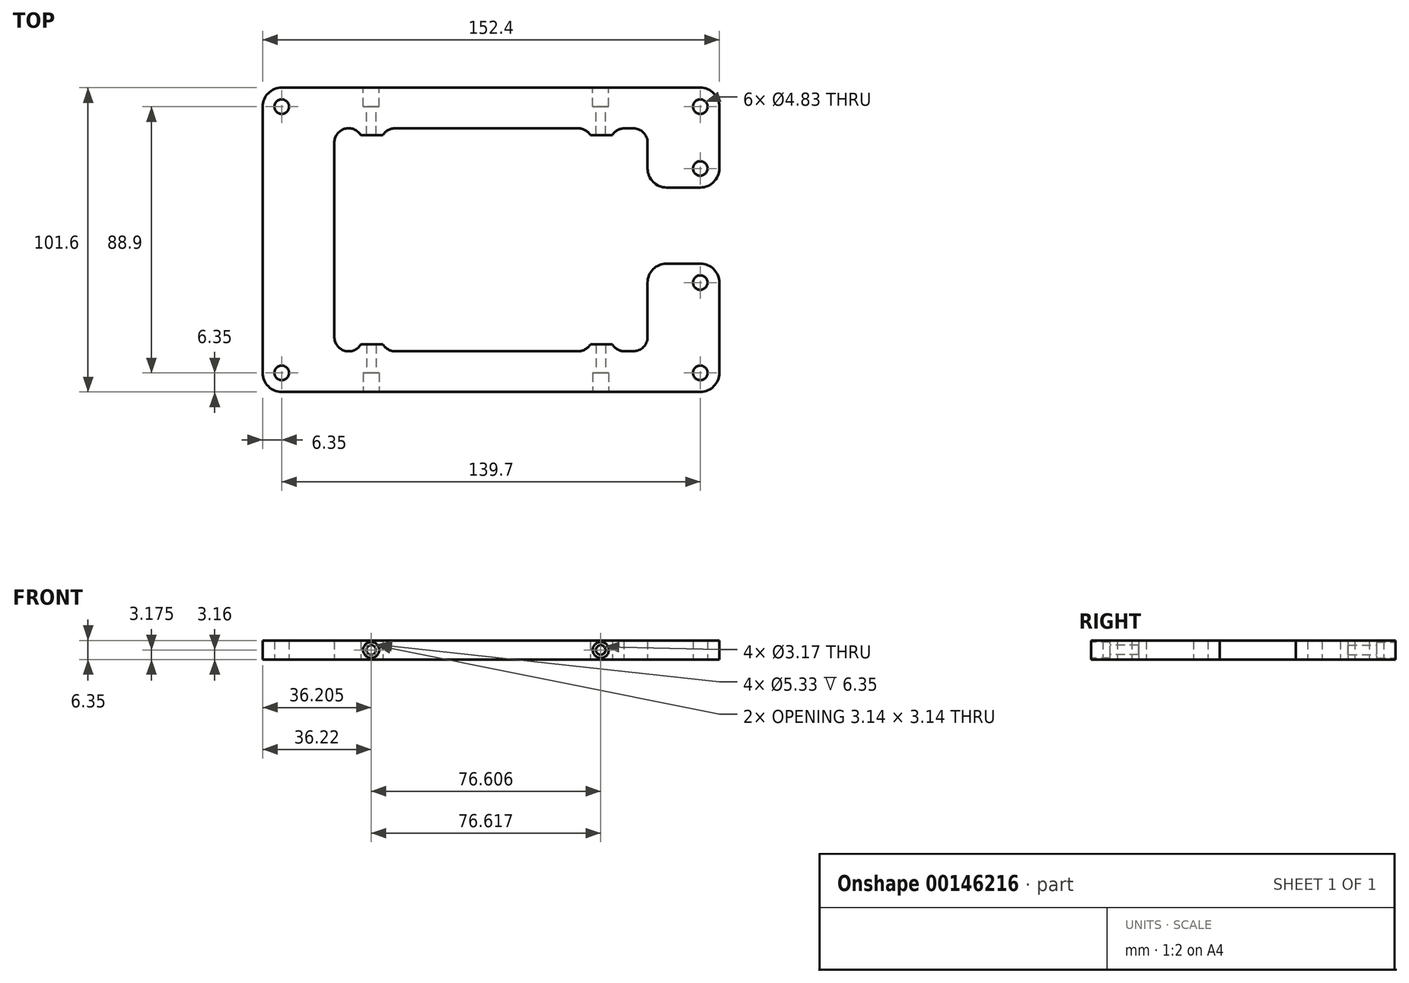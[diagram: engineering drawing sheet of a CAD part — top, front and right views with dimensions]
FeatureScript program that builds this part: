
annotation { "Feature Type Name" : "Feature", "Feature Type Description" : "" }
export const myFeature = defineFeature(function(context is Context, id is Id, definition is map)
    precondition{}
    {
        {
            var Q0;
            Q0=qCreatedBy(makeId("Top.planeOp"),FACE);
            var sketch = newSketch(context, id + "F0", { "sketchPlane" : qUnion([Q0])});
            skLineSegment(sketch, "E0.bottom", {"start": v(-69.85, 50.8) * mm, "end": v(69.85, 50.8) * mm});
            skLineSegment(sketch, "E0.top", {"start": v(-69.85, -50.8) * mm, "end": v(69.85, -50.8) * mm});
            skLineSegment(sketch, "E0.left", {"start": v(-76.2, 44.45) * mm, "end": v(-76.2, -44.45) * mm});
            skLineSegment(sketch, "E0.right", {"start": v(76.2, 44.45) * mm, "end": v(76.2, 23.81) * mm});
            skPoint(sketch, "E0.middle", {"position": v(0, 0) * mm});
            skPoint(sketch, "E1.visualSharp", {"position": v(-76.2, 50.8) * mm});
            skArc(sketch, "E1.filletArc", {"start": v(-69.85, 50.8) * mm, "mid": v(-74.34, 48.94) * mm, "end": v(-76.2, 44.45) * mm});
            skPoint(sketch, "E2.visualSharp", {"position": v(76.2, 50.8) * mm});
            skArc(sketch, "E2.filletArc", {"start": v(76.2, 44.45) * mm, "mid": v(74.34, 48.94) * mm, "end": v(69.85, 50.8) * mm});
            skPoint(sketch, "E3.visualSharp", {"position": v(76.2, -50.8) * mm});
            skArc(sketch, "E3.filletArc", {"start": v(69.85, -50.8) * mm, "mid": v(74.34, -48.94) * mm, "end": v(76.2, -44.45) * mm});
            skPoint(sketch, "E4.visualSharp", {"position": v(-76.2, -50.8) * mm});
            skArc(sketch, "E4.filletArc", {"start": v(-76.2, -44.45) * mm, "mid": v(-74.34, -48.94) * mm, "end": v(-69.85, -50.8) * mm});
            skCircle(sketch, "E5", {"center": v(-69.85, 44.45) * mm, "radius": 2.41 * mm});
            skCircle(sketch, "E6.MirrorC", {"center": v(-69.85, -44.45) * mm, "radius": 2.41 * mm});
            skCircle(sketch, "E7.MirrorC", {"center": v(69.85, -44.45) * mm, "radius": 2.41 * mm});
            skCircle(sketch, "E8.MirrorC", {"center": v(69.85, 44.45) * mm, "radius": 2.41 * mm});
            skLineSegment(sketch, "E9.top", {"start": v(0, -41.64) * mm, "end": v(0, -41.64) * mm});
            skLineSegment(sketch, "E10", {"start": v(-52.26, 32.35) * mm, "end": v(-52.26, -32.53) * mm});
            skArc(sketch, "E11", {"start": v(-43.43, 34.95) * mm, "mid": v(-48.84, 37.04) * mm, "end": v(-52.26, 32.35) * mm});
            skLineSegment(sketch, "E12", {"start": v(44.33, 37.23) * mm, "end": v(47.5, 37.23) * mm});
            skArc(sketch, "E13", {"start": v(52.26, 32.46) * mm, "mid": v(50.86, 35.83) * mm, "end": v(47.5, 37.23) * mm});
            skArc(sketch, "E14", {"start": v(44.33, 37.23) * mm, "mid": v(42.13, 36.56) * mm, "end": v(40.5, 34.94) * mm});
            skLineSegment(sketch, "E15", {"start": v(52.26, 32.46) * mm, "end": v(52.26, 23.81) * mm});
            skArc(sketch, "E16", {"start": v(33.15, 34.96) * mm, "mid": v(31.42, 36.63) * mm, "end": v(29.09, 37.24) * mm});
            skLineSegment(sketch, "E17", {"start": v(-43.43, 34.95) * mm, "end": v(-36.07, 34.95) * mm});
            skLineSegment(sketch, "E18", {"start": v(33.15, 34.96) * mm, "end": v(40.5, 34.94) * mm});
            skPoint(sketch, "E19.startSnap0", {"position": v(-32.02, 37.23) * mm});
            skPoint(sketch, "E19.endSnap0", {"position": v(29.09, 37.24) * mm});
            skArc(sketch, "E20.MirrorCS", {"start": v(44.33, -37.23) * mm, "mid": v(42.13, -36.56) * mm, "end": v(40.5, -34.94) * mm});
            skArc(sketch, "E21.MirrorCS", {"start": v(-32, -37.23) * mm, "mid": v(-34.33, -36.62) * mm, "end": v(-36.07, -34.95) * mm});
            skArc(sketch, "E22.MirrorCS", {"start": v(33.15, -34.96) * mm, "mid": v(31.42, -36.63) * mm, "end": v(29.09, -37.24) * mm});
            skLineSegment(sketch, "E23.MirrorCS", {"start": v(44.33, -37.23) * mm, "end": v(47.5, -37.23) * mm});
            skArc(sketch, "E24.MirrorCS", {"start": v(-43.43, -34.95) * mm, "mid": v(-48.84, -37.04) * mm, "end": v(-52.26, -32.35) * mm});
            skArc(sketch, "E25.MirrorCS", {"start": v(52.26, -32.46) * mm, "mid": v(50.86, -35.83) * mm, "end": v(47.5, -37.23) * mm});
            skLineSegment(sketch, "E26.MirrorCS", {"start": v(-32.02, -37.23) * mm, "end": v(29.09, -37.24) * mm});
            skPoint(sketch, "E27.MirrorP", {"position": v(-32.02, -37.23) * mm});
            skPoint(sketch, "E28.MirrorP", {"position": v(29.09, -37.24) * mm});
            skLineSegment(sketch, "E29.MirrorCS", {"start": v(33.15, -34.96) * mm, "end": v(40.5, -34.94) * mm});
            skLineSegment(sketch, "E30.MirrorCS", {"start": v(-43.43, -34.95) * mm, "end": v(-36.07, -34.95) * mm});
            skLineSegment(sketch, "E31", {"start": v(58.6, 17.46) * mm, "end": v(69.85, 17.46) * mm});
            skLineSegment(sketch, "E32", {"start": v(58.6, -7.94) * mm, "end": v(69.85, -7.94) * mm});
            skLineSegment(sketch, "E33", {"start": v(52.26, -14.29) * mm, "end": v(52.26, -32.46) * mm});
            skLineSegment(sketch, "E34", {"start": v(76.2, -14.29) * mm, "end": v(76.2, -44.45) * mm});
            skPoint(sketch, "E35.visualSharp", {"position": v(76.2, 17.46) * mm});
            skArc(sketch, "E35.filletArc", {"start": v(69.85, 17.46) * mm, "mid": v(74.34, 19.32) * mm, "end": v(76.2, 23.81) * mm});
            skPoint(sketch, "E36.visualSharp", {"position": v(76.2, -7.94) * mm});
            skArc(sketch, "E36.filletArc", {"start": v(76.2, -14.29) * mm, "mid": v(74.34, -9.8) * mm, "end": v(69.85, -7.94) * mm});
            skPoint(sketch, "E37.visualSharp", {"position": v(52.26, 17.46) * mm});
            skArc(sketch, "E37.filletArc", {"start": v(52.26, 23.81) * mm, "mid": v(54.12, 19.32) * mm, "end": v(58.6, 17.46) * mm});
            skPoint(sketch, "E38.visualSharp", {"position": v(52.26, -7.94) * mm});
            skArc(sketch, "E38.filletArc", {"start": v(58.6, -7.94) * mm, "mid": v(54.12, -9.8) * mm, "end": v(52.26, -14.29) * mm});
            skCircle(sketch, "E39", {"center": v(69.85, 23.81) * mm, "radius": 2.41 * mm});
            skCircle(sketch, "E40", {"center": v(69.85, -14.29) * mm, "radius": 2.41 * mm});
            skArc(sketch, "E41", {"start": v(-32.02, 37.23) * mm, "mid": v(-34.35, 36.62) * mm, "end": v(-36.08, 34.95) * mm});
            skLineSegment(sketch, "E42", {"start": v(-32.02, 37.23) * mm, "end": v(29.09, 37.24) * mm});
            skPoint(sketch, "E43.endSnap0", {"position": v(0, 50.8) * mm});
            skLineSegment(sketch, "E44", {"start": v(-76.2, 0) * mm, "end": v(76.2, 0) * mm, "construction": true});
            skSolve(sketch);
        }
        {
            var Q0;
            Q0 = qSketchRegion(id + "F0", true);
            extrude(context, id + "F1", {"entities" : qUnion([Q0]), "depth" : 6.35 * mm});
        }
        {
            var Q0;
            Q0=makeQuery(id+"F1.opExtrude","SWEPT_FACE",FACE,{"disambiguationData":[OSD([sQuery(id+"F0.wireOp",EDGE,"E0.top")])]});
            var sketch = newSketch(context, id + "F2", { "sketchPlane" : qUnion([Q0])});
            skPoint(sketch, "E45", {"position": v(-39.98, 3.18) * mm});
            skPoint(sketch, "E46", {"position": v(36.64, 3.18) * mm});
            skSolve(sketch);
        }
        {
            var Q0;
            Q0=sQuery(id+"F2.wireOp",VERTEX,"E45");
            var Q1;
            Q1=sQuery(id+"F2.wireOp",VERTEX,"E46");
            var Q2;
            Q2=makeQuery(id+"F1.opExtrude","SWEPT_BODY",BODY,{"disambiguationData":[OSD([sQuery(id+"F0.wireOp",EDGE,"E0.bottom"),sQuery(id+"F0.wireOp",EDGE,"E0.top"),sQuery(id+"F0.wireOp",EDGE,"E0.left"),sQuery(id+"F0.wireOp",EDGE,"E0.right"),sQuery(id+"F0.wireOp",EDGE,"E1.filletArc"),sQuery(id+"F0.wireOp",EDGE,"E2.filletArc"),sQuery(id+"F0.wireOp",EDGE,"E3.filletArc"),sQuery(id+"F0.wireOp",EDGE,"E4.filletArc"),sQuery(id+"F0.wireOp",EDGE,"E6.MirrorC"),sQuery(id+"F0.wireOp",EDGE,"E5"),sQuery(id+"F0.wireOp",EDGE,"E7.MirrorC"),sQuery(id+"F0.wireOp",EDGE,"E8.MirrorC"),sQuery(id+"F0.wireOp",EDGE,"E10"),sQuery(id+"F0.wireOp",EDGE,"E11"),sQuery(id+"F0.wireOp",EDGE,"E12"),sQuery(id+"F0.wireOp",EDGE,"E13"),sQuery(id+"F0.wireOp",EDGE,"E14"),sQuery(id+"F0.wireOp",EDGE,"E15"),sQuery(id+"F0.wireOp",EDGE,"E16"),sQuery(id+"F0.wireOp",EDGE,"E17"),sQuery(id+"F0.wireOp",EDGE,"E18"),sQuery(id+"F0.wireOp",EDGE,"E20.MirrorCS"),sQuery(id+"F0.wireOp",EDGE,"E21.MirrorCS"),sQuery(id+"F0.wireOp",EDGE,"E22.MirrorCS"),sQuery(id+"F0.wireOp",EDGE,"E23.MirrorCS"),sQuery(id+"F0.wireOp",EDGE,"E24.MirrorCS"),sQuery(id+"F0.wireOp",EDGE,"E25.MirrorCS"),sQuery(id+"F0.wireOp",EDGE,"E26.MirrorCS"),sQuery(id+"F0.wireOp",EDGE,"E29.MirrorCS"),sQuery(id+"F0.wireOp",EDGE,"E30.MirrorCS"),sQuery(id+"F0.wireOp",EDGE,"E31"),sQuery(id+"F0.wireOp",EDGE,"E32"),sQuery(id+"F0.wireOp",EDGE,"E33"),sQuery(id+"F0.wireOp",EDGE,"E34"),sQuery(id+"F0.wireOp",EDGE,"E35.filletArc"),sQuery(id+"F0.wireOp",EDGE,"E36.filletArc"),sQuery(id+"F0.wireOp",EDGE,"E37.filletArc"),sQuery(id+"F0.wireOp",EDGE,"E38.filletArc"),sQuery(id+"F0.wireOp",EDGE,"E39"),sQuery(id+"F0.wireOp",EDGE,"E40"),sQuery(id+"F0.wireOp",EDGE,"E41"),sQuery(id+"F0.wireOp",EDGE,"E42")])]});
            hole(context, id + "F3", {"style" : HoleStyle.C_BORE, "endStyle" : HoleEndStyle.BLIND, "holeDiameter" : 3.17 * mm, "cBoreDiameter" : 5.33 * mm, "cBoreDepth" : 6.35 * mm, "holeDepth" : 15.88 * mm, "locations" : qUnion([Q0, Q1]), "scope" : qUnion([Q2])});
        }
        {
            var Q0;
            Q0=makeQuery(id+"F1.opExtrude","SWEPT_FACE",FACE,{"disambiguationData":[OSD([sQuery(id+"F0.wireOp",EDGE,"E0.bottom")])]});
            var sketch = newSketch(context, id + "F4", { "sketchPlane" : qUnion([Q0])});
            skPoint(sketch, "E47", {"position": v(39.98, 3.18) * mm});
            skPoint(sketch, "E48", {"position": v(-36.63, 3.18) * mm});
            skSolve(sketch);
        }
        {
            var Q0;
            Q0=sQuery(id+"F4.wireOp",VERTEX,"E48");
            var Q1;
            Q1=sQuery(id+"F4.wireOp",VERTEX,"E47");
            var Q2;
            Q2=makeQuery(id+"F1.opExtrude","SWEPT_BODY",BODY,{"disambiguationData":[OSD([sQuery(id+"F0.wireOp",EDGE,"E0.bottom"),sQuery(id+"F0.wireOp",EDGE,"E0.top"),sQuery(id+"F0.wireOp",EDGE,"E0.left"),sQuery(id+"F0.wireOp",EDGE,"E0.right"),sQuery(id+"F0.wireOp",EDGE,"E1.filletArc"),sQuery(id+"F0.wireOp",EDGE,"E2.filletArc"),sQuery(id+"F0.wireOp",EDGE,"E3.filletArc"),sQuery(id+"F0.wireOp",EDGE,"E4.filletArc"),sQuery(id+"F0.wireOp",EDGE,"E6.MirrorC"),sQuery(id+"F0.wireOp",EDGE,"E5"),sQuery(id+"F0.wireOp",EDGE,"E7.MirrorC"),sQuery(id+"F0.wireOp",EDGE,"E8.MirrorC"),sQuery(id+"F0.wireOp",EDGE,"E10"),sQuery(id+"F0.wireOp",EDGE,"E11"),sQuery(id+"F0.wireOp",EDGE,"E12"),sQuery(id+"F0.wireOp",EDGE,"E13"),sQuery(id+"F0.wireOp",EDGE,"E14"),sQuery(id+"F0.wireOp",EDGE,"E15"),sQuery(id+"F0.wireOp",EDGE,"E16"),sQuery(id+"F0.wireOp",EDGE,"E17"),sQuery(id+"F0.wireOp",EDGE,"E18"),sQuery(id+"F0.wireOp",EDGE,"E20.MirrorCS"),sQuery(id+"F0.wireOp",EDGE,"E21.MirrorCS"),sQuery(id+"F0.wireOp",EDGE,"E22.MirrorCS"),sQuery(id+"F0.wireOp",EDGE,"E23.MirrorCS"),sQuery(id+"F0.wireOp",EDGE,"E24.MirrorCS"),sQuery(id+"F0.wireOp",EDGE,"E25.MirrorCS"),sQuery(id+"F0.wireOp",EDGE,"E26.MirrorCS"),sQuery(id+"F0.wireOp",EDGE,"E29.MirrorCS"),sQuery(id+"F0.wireOp",EDGE,"E30.MirrorCS"),sQuery(id+"F0.wireOp",EDGE,"E31"),sQuery(id+"F0.wireOp",EDGE,"E32"),sQuery(id+"F0.wireOp",EDGE,"E33"),sQuery(id+"F0.wireOp",EDGE,"E34"),sQuery(id+"F0.wireOp",EDGE,"E35.filletArc"),sQuery(id+"F0.wireOp",EDGE,"E36.filletArc"),sQuery(id+"F0.wireOp",EDGE,"E37.filletArc"),sQuery(id+"F0.wireOp",EDGE,"E38.filletArc"),sQuery(id+"F0.wireOp",EDGE,"E39"),sQuery(id+"F0.wireOp",EDGE,"E40"),sQuery(id+"F0.wireOp",EDGE,"E41"),sQuery(id+"F0.wireOp",EDGE,"E42")])]});
            hole(context, id + "F5", {"style" : HoleStyle.C_BORE, "endStyle" : HoleEndStyle.BLIND, "holeDiameter" : 3.17 * mm, "cBoreDiameter" : 5.33 * mm, "cBoreDepth" : 6.35 * mm, "holeDepth" : 15.88 * mm, "locations" : qUnion([Q0, Q1]), "scope" : qUnion([Q2])});
        }
    });
